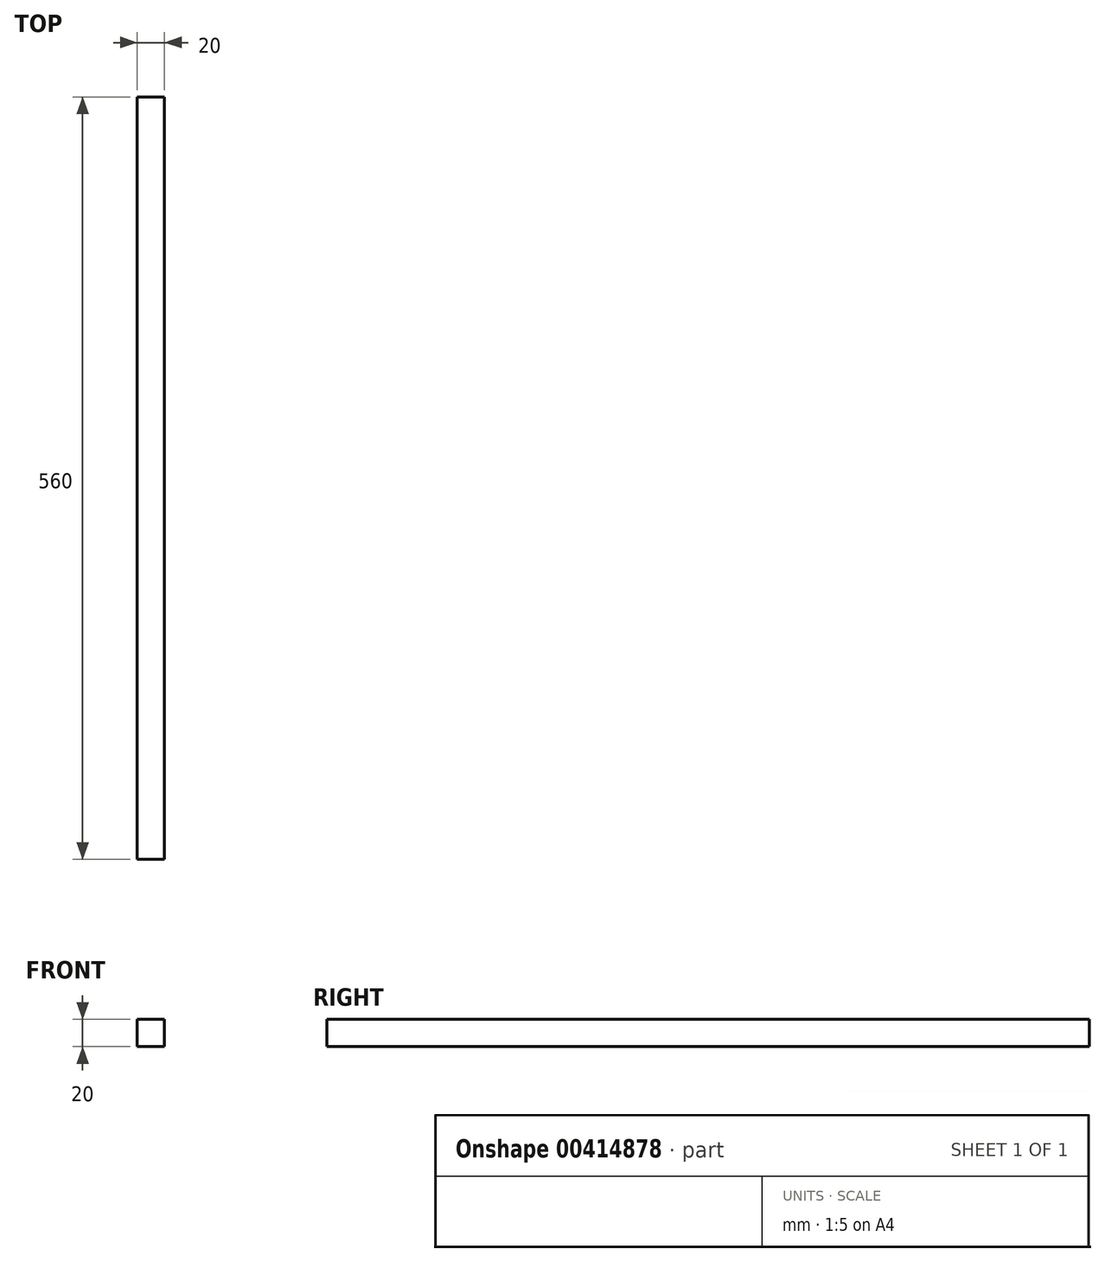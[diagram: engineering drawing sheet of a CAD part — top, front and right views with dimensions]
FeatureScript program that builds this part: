
annotation { "Feature Type Name" : "Feature", "Feature Type Description" : "" }
export const myFeature = defineFeature(function(context is Context, id is Id, definition is map)
    precondition{}
    {
        {
            var Q0;
            Q0=qCreatedBy(makeId("Front.planeOp"),FACE);
            var sketch = newSketch(context, id + "F0", { "sketchPlane" : qUnion([Q0])});
            skLineSegment(sketch, "E0.bottom", {"start": v(-10, 20) * mm, "end": v(10, 20) * mm});
            skLineSegment(sketch, "E0.top", {"start": v(-10, 0) * mm, "end": v(10, 0) * mm});
            skLineSegment(sketch, "E0.left", {"start": v(-10, 20) * mm, "end": v(-10, 0) * mm});
            skLineSegment(sketch, "E0.right", {"start": v(10, 20) * mm, "end": v(10, 0) * mm});
            skSolve(sketch);
        }
        {
            var Q0;
            Q0=makeQuery(id+"F0.imprint","IMPRINT",FACE,{"disambiguationData":[TD([[makeQuery(id+"F0.imprint","IMPRINT",EDGE,{"derivedFrom":sQuery(id+"F0.wireOp",EDGE,"E0.bottom")}),-1.0]])]});
            extrude(context, id + "F1", {"entities" : qUnion([Q0]), "endBound" : BoundingType.SYMMETRIC, "depth" : 560 * mm});
        }
    });
